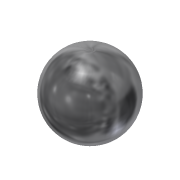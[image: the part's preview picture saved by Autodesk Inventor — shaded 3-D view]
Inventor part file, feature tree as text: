
AUTODESK INVENTOR PART (.ipt)
format: ipt  version: 2014 (Build 180170000, 170)  size: 123,392 bytes
history: native  units: mm
features: sketch x2, revolve x1, hole x1, chamfer x1
ambient origin geometry x8: Origin, YZ Plane, XZ Plane, XY Plane, X Axis, Y Axis, Z Axis, Center Point
bodies: Body1 (feature_tree)
feature tree (5):
  revolve  "Revolution1"  [1 undecoded]
  hole  "Hole1"  [1 undecoded]
  chamfer  "Chamfer1"  [1 undecoded]
  sketch  "Sketch5"  dims[d15=10.0mm d16=9.2mm]
  sketch  "Sketch6"  dims[d17=90.0deg d18=3.242mm d19=6.0mm d20=4.0mm d21=2.0mm d22=90.0deg d23=7.0mm d24=20.594885mm d25=0.3mm d26=2.0mm d27=45.0deg]
note: 3 required parameter values undecoded (feature->parameter linkage not recoverable at this tier; creation-order binding heuristic only, values carry confidence <= 0.55)